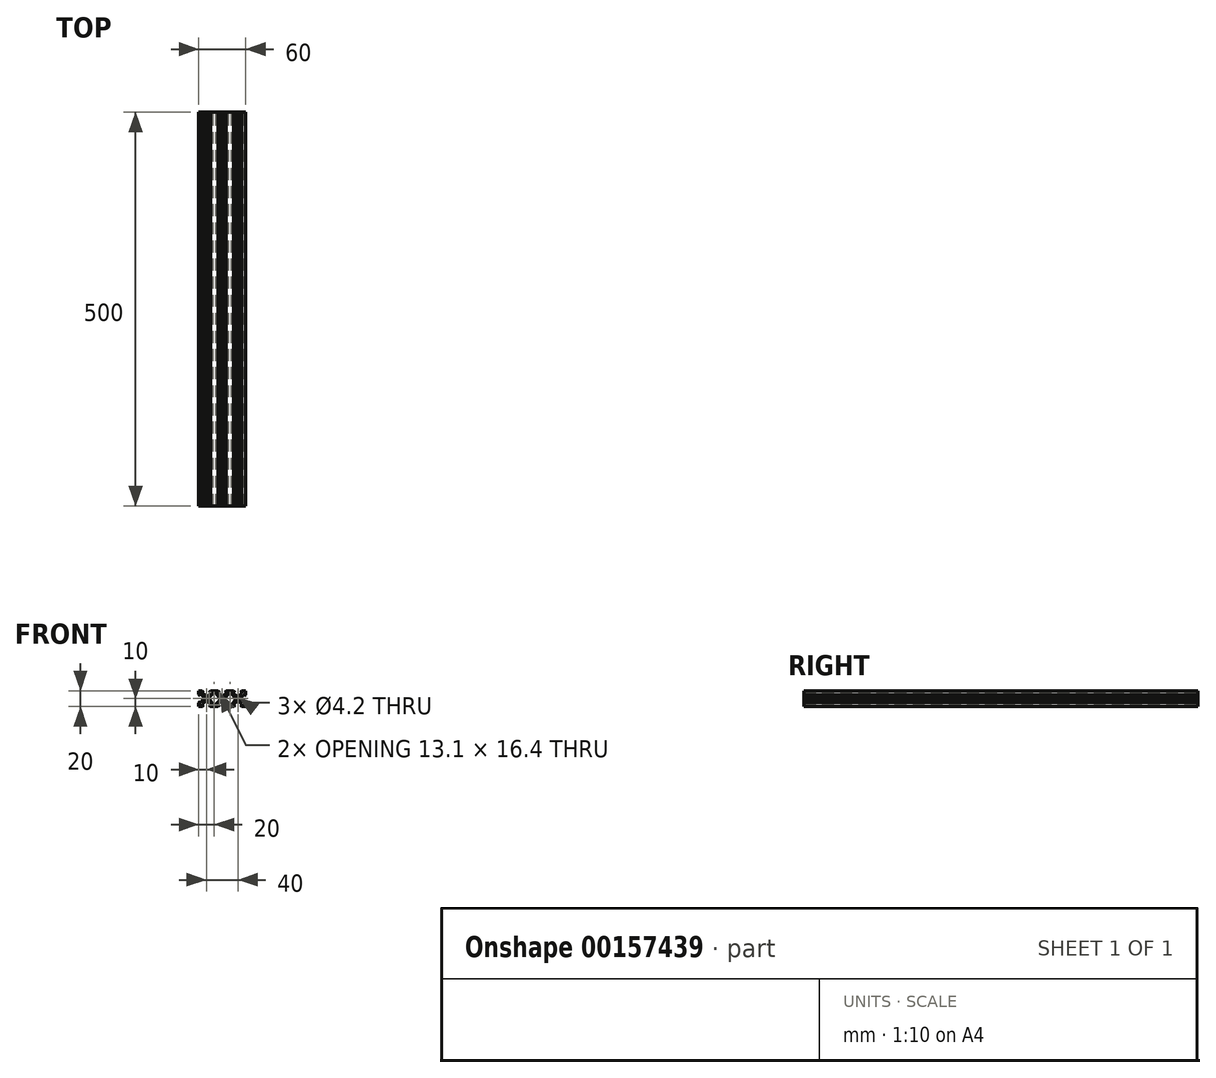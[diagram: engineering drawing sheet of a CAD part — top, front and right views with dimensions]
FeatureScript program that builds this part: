
annotation { "Feature Type Name" : "Feature", "Feature Type Description" : "" }
export const myFeature = defineFeature(function(context is Context, id is Id, definition is map)
    precondition{}
    {
        {
            var Q0;
            Q0=qCreatedBy(makeId("Front.planeOp"),FACE);
            var sketch = newSketch(context, id + "F0", { "sketchPlane" : qUnion([Q0])});
            skLineSegment(sketch, "E0.bottom", {"start": v(30, 10) * mm, "end": v(24.82, 10) * mm});
            skLineSegment(sketch, "E0.top", {"start": v(30, -10) * mm, "end": v(24.78, -10) * mm});
            skLineSegment(sketch, "E0.left", {"start": v(30, 10) * mm, "end": v(30, 4.8) * mm});
            skLineSegment(sketch, "E0.right", {"start": v(-30, 10) * mm, "end": v(-30, 5.17) * mm});
            skPoint(sketch, "E0.middle", {"position": v(0, 0) * mm});
            skLineSegment(sketch, "E1.0", {"start": v(-28.2, 8.2) * mm, "end": v(-28.2, 3.63) * mm});
            skLineSegment(sketch, "E1.1", {"start": v(28.2, 8.2) * mm, "end": v(23.56, 8.2) * mm});
            skLineSegment(sketch, "E1.2", {"start": v(28.2, 8.2) * mm, "end": v(28.2, 3.44) * mm});
            skLineSegment(sketch, "E1.3", {"start": v(28.2, -8.2) * mm, "end": v(23.52, -8.2) * mm});
            skCircle(sketch, "E2", {"center": v(0, 0) * mm, "radius": 2.1 * mm});
            skCircle(sketch, "E3", {"center": v(-20, 0) * mm, "radius": 2.1 * mm});
            skCircle(sketch, "E4", {"center": v(20, 0) * mm, "radius": 2.1 * mm});
            skLineSegment(sketch, "E5", {"start": v(-30, 5.17) * mm, "end": v(-28.2, 3.63) * mm});
            skLineSegment(sketch, "E6", {"start": v(-30, -5.22) * mm, "end": v(-28.2, -3.47) * mm});
            skLineSegment(sketch, "E7", {"start": v(-25.2, 10) * mm, "end": v(-23.47, 8.2) * mm});
            skLineSegment(sketch, "E8", {"start": v(-16.45, 8.2) * mm, "end": v(-14.84, 10) * mm});
            skLineSegment(sketch, "E9", {"start": v(-24.81, -10) * mm, "end": v(-23.55, -8.2) * mm});
            skLineSegment(sketch, "E10", {"start": v(-16.57, -8.2) * mm, "end": v(-15.34, -10) * mm});
            skLineSegment(sketch, "E11", {"start": v(3.5, 8.2) * mm, "end": v(5.22, 10) * mm});
            skLineSegment(sketch, "E12", {"start": v(-4.91, -10) * mm, "end": v(-3.52, -8.2) * mm});
            skLineSegment(sketch, "E13", {"start": v(3.53, -8.2) * mm, "end": v(5.18, -10) * mm});
            skLineSegment(sketch, "E14", {"start": v(14.8, 10) * mm, "end": v(16.37, 8.2) * mm});
            skLineSegment(sketch, "E15", {"start": v(23.56, 8.2) * mm, "end": v(24.82, 10) * mm});
            skLineSegment(sketch, "E16", {"start": v(15.3, -10) * mm, "end": v(16.45, -8.2) * mm});
            skLineSegment(sketch, "E17", {"start": v(23.52, -8.2) * mm, "end": v(24.78, -10) * mm});
            skLineSegment(sketch, "E18", {"start": v(28.2, -3.58) * mm, "end": v(30, -5.08) * mm});
            skLineSegment(sketch, "E19", {"start": v(28.2, 3.44) * mm, "end": v(30, 4.8) * mm});
            skLineSegment(sketch, "E20.bottom", {"start": v(-16.55, 3.45) * mm, "end": v(-23.45, 3.45) * mm});
            skLineSegment(sketch, "E20.top", {"start": v(-16.55, -3.45) * mm, "end": v(-23.45, -3.45) * mm});
            skLineSegment(sketch, "E20.left", {"start": v(-16.55, 3.45) * mm, "end": v(-16.55, -3.45) * mm});
            skLineSegment(sketch, "E20.right", {"start": v(-23.45, 3.45) * mm, "end": v(-23.45, -3.45) * mm});
            skLineSegment(sketch, "E21.bottom", {"start": v(3.45, 3.45) * mm, "end": v(-3.45, 3.45) * mm});
            skLineSegment(sketch, "E21.top", {"start": v(3.45, -3.45) * mm, "end": v(-3.45, -3.45) * mm});
            skLineSegment(sketch, "E21.left", {"start": v(3.45, 3.45) * mm, "end": v(3.45, -3.45) * mm});
            skLineSegment(sketch, "E21.right", {"start": v(-3.45, 3.45) * mm, "end": v(-3.45, -3.45) * mm});
            skLineSegment(sketch, "E22.bottom", {"start": v(23.45, 3.45) * mm, "end": v(16.55, 3.45) * mm});
            skLineSegment(sketch, "E22.top", {"start": v(23.45, -3.45) * mm, "end": v(16.55, -3.45) * mm});
            skLineSegment(sketch, "E22.left", {"start": v(23.45, 3.45) * mm, "end": v(23.45, -3.45) * mm});
            skLineSegment(sketch, "E22.right", {"start": v(16.55, 3.45) * mm, "end": v(16.55, -3.45) * mm});
            skLineSegment(sketch, "E23", {"start": v(-20, 2.1) * mm, "end": v(-44.26, 2.1) * mm, "construction": true});
            skPoint(sketch, "E23.startSnap0", {"position": v(-20, 3.45) * mm});
            skLineSegment(sketch, "E24", {"start": v(-19.99, -2.1) * mm, "end": v(-43.86, -2.1) * mm, "construction": true});
            skLineSegment(sketch, "E25.0", {"start": v(-26.56, 6.56) * mm, "end": v(-26.56, 5.22) * mm});
            skLineSegment(sketch, "E25.1", {"start": v(26.56, 6.56) * mm, "end": v(24.86, 6.56) * mm});
            skLineSegment(sketch, "E25.2", {"start": v(26.56, 6.56) * mm, "end": v(26.56, 4.87) * mm});
            skLineSegment(sketch, "E25.3", {"start": v(26.56, -6.56) * mm, "end": v(24.85, -6.56) * mm});
            skLineSegment(sketch, "E26", {"start": v(-25.16, 6.56) * mm, "end": v(-25.16, 8.2) * mm});
            skLineSegment(sketch, "E27", {"start": v(-26.56, 5.22) * mm, "end": v(-28.2, 5.22) * mm});
            skLineSegment(sketch, "E28", {"start": v(-25.16, 6.56) * mm, "end": v(-20.7, 3.45) * mm});
            skLineSegment(sketch, "E29", {"start": v(-26.56, 5.22) * mm, "end": v(-23.45, 2.06) * mm});
            skLineSegment(sketch, "E30", {"start": v(-26.56, -5.26) * mm, "end": v(-23.45, -0.51) * mm});
            skLineSegment(sketch, "E31", {"start": v(-24.87, -6.56) * mm, "end": v(-21.77, -3.45) * mm});
            skLineSegment(sketch, "E32", {"start": v(-26.56, -5.26) * mm, "end": v(-28.2, -5.26) * mm});
            skLineSegment(sketch, "E33", {"start": v(-24.87, -6.56) * mm, "end": v(-24.87, -8.2) * mm});
            skLineSegment(sketch, "E34", {"start": v(-14.83, 8.2) * mm, "end": v(-14.83, 6.56) * mm});
            skLineSegment(sketch, "E35", {"start": v(-14.83, 6.56) * mm, "end": v(-18, 3.45) * mm});
            skLineSegment(sketch, "E36", {"start": v(-16.55, 1.87) * mm, "end": v(-11.8, 6.56) * mm});
            skLineSegment(sketch, "E37", {"start": v(-3.48, 8.2) * mm, "end": v(-4.91, 10) * mm});
            skLineSegment(sketch, "E38", {"start": v(-19.34, -3.45) * mm, "end": v(-15.36, -6.56) * mm});
            skLineSegment(sketch, "E39", {"start": v(-15.36, -6.56) * mm, "end": v(-15.36, -8.2) * mm});
            skLineSegment(sketch, "E40", {"start": v(-16.55, -0.63) * mm, "end": v(-12.6, -6.56) * mm});
            skLineSegment(sketch, "E41", {"start": v(-1.9, 3.45) * mm, "end": v(-4.8, 6.56) * mm});
            skLineSegment(sketch, "E42", {"start": v(-4.8, 6.56) * mm, "end": v(-4.8, 8.2) * mm});
            skLineSegment(sketch, "E43", {"start": v(-3.45, 0.53) * mm, "end": v(-7.5, 6.56) * mm});
            skLineSegment(sketch, "E44", {"start": v(-3.45, -2.14) * mm, "end": v(-7.78, -6.56) * mm});
            skLineSegment(sketch, "E45", {"start": v(-1.46, -3.45) * mm, "end": v(-5.05, -6.56) * mm});
            skLineSegment(sketch, "E46", {"start": v(-5.05, -6.56) * mm, "end": v(-5.05, -8.2) * mm});
            skLineSegment(sketch, "E47", {"start": v(-12.6, -6.56) * mm, "end": v(-12.6, -8.2) * mm});
            skLineSegment(sketch, "E48", {"start": v(-7.78, -6.56) * mm, "end": v(-7.78, -8.2) * mm});
            skLineSegment(sketch, "E49", {"start": v(-7.5, 6.56) * mm, "end": v(-7.5, 8.2) * mm});
            skLineSegment(sketch, "E50", {"start": v(-11.8, 6.56) * mm, "end": v(-11.8, 8.2) * mm});
            skLineSegment(sketch, "E51", {"start": v(0.74, 3.45) * mm, "end": v(5.08, 6.56) * mm});
            skLineSegment(sketch, "E52", {"start": v(3.45, 0.52) * mm, "end": v(8.04, 6.56) * mm});
            skLineSegment(sketch, "E53", {"start": v(8.04, 6.56) * mm, "end": v(8.04, 8.2) * mm});
            skLineSegment(sketch, "E54", {"start": v(1.52, -3.45) * mm, "end": v(5.2, -6.56) * mm});
            skLineSegment(sketch, "E55", {"start": v(5.2, -6.56) * mm, "end": v(5.2, -8.2) * mm});
            skLineSegment(sketch, "E56", {"start": v(3.45, -1.7) * mm, "end": v(7.97, -6.56) * mm});
            skLineSegment(sketch, "E57", {"start": v(18.15, 3.45) * mm, "end": v(14.79, 6.56) * mm});
            skLineSegment(sketch, "E58", {"start": v(16.55, 0.58) * mm, "end": v(12.18, 6.56) * mm});
            skLineSegment(sketch, "E59", {"start": v(12.18, 6.56) * mm, "end": v(12.18, 8.2) * mm});
            skLineSegment(sketch, "E60", {"start": v(14.79, 6.56) * mm, "end": v(14.79, 8.2) * mm});
            skLineSegment(sketch, "E61", {"start": v(16.55, -2.05) * mm, "end": v(12.38, -6.56) * mm});
            skLineSegment(sketch, "E62", {"start": v(18.78, -3.45) * mm, "end": v(15.16, -6.56) * mm});
            skLineSegment(sketch, "E63", {"start": v(12.38, -6.56) * mm, "end": v(12.38, -8.2) * mm});
            skLineSegment(sketch, "E64", {"start": v(20.78, 3.45) * mm, "end": v(24.86, 6.56) * mm});
            skLineSegment(sketch, "E65", {"start": v(23.45, 0.43) * mm, "end": v(26.56, 4.87) * mm});
            skLineSegment(sketch, "E66", {"start": v(23.45, -1.97) * mm, "end": v(26.56, -5.05) * mm});
            skLineSegment(sketch, "E67", {"start": v(26.56, -5.05) * mm, "end": v(28.2, -5.05) * mm});
            skLineSegment(sketch, "E68", {"start": v(21.27, -3.45) * mm, "end": v(24.85, -6.56) * mm});
            skLineSegment(sketch, "E69", {"start": v(24.85, -6.56) * mm, "end": v(24.85, -8.2) * mm});
            skLineSegment(sketch, "E70.trimOffspring", {"start": v(-25.2, 10) * mm, "end": v(-30, 10) * mm});
            skLineSegment(sketch, "E71.trimOffspring", {"start": v(-23.47, 8.2) * mm, "end": v(-28.2, 8.2) * mm});
            skLineSegment(sketch, "E72.trimOffspring", {"start": v(-25.16, 6.56) * mm, "end": v(-26.56, 6.56) * mm});
            skLineSegment(sketch, "E73.trimOffspring", {"start": v(-28.2, -3.47) * mm, "end": v(-28.2, -8.2) * mm});
            skLineSegment(sketch, "E74.trimOffspring", {"start": v(-30, -5.22) * mm, "end": v(-30, -10) * mm});
            skLineSegment(sketch, "E75.trimOffspring", {"start": v(-26.56, -5.26) * mm, "end": v(-26.56, -6.56) * mm});
            skLineSegment(sketch, "E76.trimOffspring", {"start": v(-11.8, 6.56) * mm, "end": v(-14.83, 6.56) * mm});
            skLineSegment(sketch, "E77.trimOffspring", {"start": v(-12.6, -6.56) * mm, "end": v(-15.36, -6.56) * mm});
            skLineSegment(sketch, "E78.trimOffspring", {"start": v(-24.87, -6.56) * mm, "end": v(-26.56, -6.56) * mm});
            skLineSegment(sketch, "E79.trimOffspring", {"start": v(-23.55, -8.2) * mm, "end": v(-28.2, -8.2) * mm});
            skLineSegment(sketch, "E80.trimOffspring", {"start": v(-24.81, -10) * mm, "end": v(-30, -10) * mm});
            skLineSegment(sketch, "E81.trimOffspring", {"start": v(-4.91, 10) * mm, "end": v(-14.84, 10) * mm});
            skLineSegment(sketch, "E82", {"start": v(5.08, 6.56) * mm, "end": v(5.08, 8.2) * mm});
            skLineSegment(sketch, "E83.trimOffspring", {"start": v(-3.48, 8.2) * mm, "end": v(-16.45, 8.2) * mm});
            skLineSegment(sketch, "E84.trimOffspring", {"start": v(-4.8, 6.56) * mm, "end": v(-7.5, 6.56) * mm});
            skLineSegment(sketch, "E85.trimOffspring", {"start": v(8.04, 6.56) * mm, "end": v(5.08, 6.56) * mm});
            skLineSegment(sketch, "E86.trimOffspring", {"start": v(7.97, -6.56) * mm, "end": v(5.2, -6.56) * mm});
            skLineSegment(sketch, "E87.trimOffspring", {"start": v(-4.91, -10) * mm, "end": v(-15.34, -10) * mm});
            skLineSegment(sketch, "E88.trimOffspring", {"start": v(-3.52, -8.2) * mm, "end": v(-16.57, -8.2) * mm});
            skLineSegment(sketch, "E89.trimOffspring", {"start": v(-5.05, -6.56) * mm, "end": v(-7.78, -6.56) * mm});
            skLineSegment(sketch, "E90.trimOffspring", {"start": v(15.3, -10) * mm, "end": v(5.18, -10) * mm});
            skLineSegment(sketch, "E91", {"start": v(15.16, -6.56) * mm, "end": v(15.16, -8.2) * mm});
            skLineSegment(sketch, "E92.trimOffspring", {"start": v(16.45, -8.2) * mm, "end": v(3.53, -8.2) * mm});
            skLineSegment(sketch, "E93.trimOffspring", {"start": v(15.16, -6.56) * mm, "end": v(12.38, -6.56) * mm});
            skLineSegment(sketch, "E94.trimOffspring", {"start": v(30, -5.08) * mm, "end": v(30, -10) * mm});
            skLineSegment(sketch, "E95.trimOffspring", {"start": v(28.2, -3.58) * mm, "end": v(28.2, -8.2) * mm});
            skLineSegment(sketch, "E96.trimOffspring", {"start": v(26.56, -5.05) * mm, "end": v(26.56, -6.56) * mm});
            skLineSegment(sketch, "E97", {"start": v(24.86, 6.56) * mm, "end": v(24.86, 8.2) * mm});
            skLineSegment(sketch, "E98", {"start": v(26.56, 4.87) * mm, "end": v(28.2, 4.87) * mm});
            skLineSegment(sketch, "E99.trimOffspring", {"start": v(14.8, 10) * mm, "end": v(5.22, 10) * mm});
            skLineSegment(sketch, "E100.trimOffspring", {"start": v(16.37, 8.2) * mm, "end": v(3.5, 8.2) * mm});
            skLineSegment(sketch, "E101.trimOffspring", {"start": v(14.79, 6.56) * mm, "end": v(12.18, 6.56) * mm});
            skLineSegment(sketch, "E102", {"start": v(7.97, -6.56) * mm, "end": v(7.97, -8.2) * mm});
            skSolve(sketch);
        }
        {
            var Q0;
            Q0=makeQuery(id+"F0.imprint","IMPRINT",FACE,{"disambiguationData":[TD([[makeQuery(id+"F0.imprint","IMPRINT",EDGE,{"derivedFrom":sQuery(id+"F0.wireOp",EDGE,"E0.bottom")}),1.0]])]});
            var Q1;
            Q1=makeQuery(id+"F0.imprint","IMPRINT",FACE,{"disambiguationData":[TD([[makeQuery(id+"F0.imprint","IMPRINT",EDGE,{"derivedFrom":sQuery(id+"F0.wireOp",EDGE,"E25.1")}),-1.0]])]});
            var Q2;
            Q2=makeQuery(id+"F0.imprint","IMPRINT",FACE,{"disambiguationData":[TD([[makeQuery(id+"F0.imprint","IMPRINT",EDGE,{"derivedFrom":sQuery(id+"F0.wireOp",EDGE,"E25.1")}),1.0]])]});
            var Q3;
            {var subQ1=sQuery(id+"F0.wireOp",EDGE,"E25.3");Q3=makeQuery(id+"F0.imprint","IMPRINT",FACE,{"disambiguationData":[TD([[makeQuery(id+"F0.imprint","IMPRINT",EDGE,{"derivedFrom":subQ1}),1.0]])]});}
            var Q4;
            Q4=makeQuery(id+"F0.imprint","IMPRINT",FACE,{"disambiguationData":[TD([[makeQuery(id+"F0.imprint","IMPRINT",EDGE,{"derivedFrom":sQuery(id+"F0.wireOp",EDGE,"E0.top")}),-1.0]])]});
            var Q5;
            Q5=makeQuery(id+"F0.imprint","IMPRINT",FACE,{"disambiguationData":[TD([[makeQuery(id+"F0.imprint","IMPRINT",EDGE,{"derivedFrom":sQuery(id+"F0.wireOp",EDGE,"E25.3")}),-1.0]])]});
            var Q6;
            Q6=makeQuery(id+"F0.imprint","IMPRINT",FACE,{"disambiguationData":[TD([[makeQuery(id+"F0.imprint","IMPRINT",EDGE,{"derivedFrom":sQuery(id+"F0.wireOp",EDGE,"E4")}),-1.0]])]});
            var Q7;
            {var subQ1=sQuery(id+"F0.wireOp",EDGE,"E57");Q7=makeQuery(id+"F0.imprint","IMPRINT",FACE,{"disambiguationData":[TD([[makeQuery(id+"F0.imprint","IMPRINT",EDGE,{"derivedFrom":subQ1}),1.0]])]});}
            var Q8;
            {var subQ4=sQuery(id+"F0.wireOp",EDGE,"E60");Q8=makeQuery(id+"F0.imprint","IMPRINT",FACE,{"disambiguationData":[TD([[makeQuery(id+"F0.imprint","IMPRINT",EDGE,{"derivedFrom":subQ4}),1.0]])]});}
            var Q9;
            {var subQ3=sQuery(id+"F0.wireOp",EDGE,"E11");Q9=makeQuery(id+"F0.imprint","IMPRINT",FACE,{"disambiguationData":[TD([[makeQuery(id+"F0.imprint","IMPRINT",EDGE,{"derivedFrom":subQ3}),-1.0]])]});}
            var Q10;
            {var subQ0=sQuery(id+"F0.wireOp",EDGE,"E53");Q10=makeQuery(id+"F0.imprint","IMPRINT",FACE,{"disambiguationData":[TD([[makeQuery(id+"F0.imprint","IMPRINT",EDGE,{"derivedFrom":subQ0}),1.0]])]});}
            var Q11;
            {var subQ1=sQuery(id+"F0.wireOp",EDGE,"E51");Q11=makeQuery(id+"F0.imprint","IMPRINT",FACE,{"disambiguationData":[TD([[makeQuery(id+"F0.imprint","IMPRINT",EDGE,{"derivedFrom":subQ1}),-1.0]])]});}
            var Q12;
            {var subQ4=sQuery(id+"F0.wireOp",EDGE,"E61");Q12=makeQuery(id+"F0.imprint","IMPRINT",FACE,{"disambiguationData":[TD([[makeQuery(id+"F0.imprint","IMPRINT",EDGE,{"derivedFrom":subQ4}),1.0]])]});}
            var Q13;
            {var subQ0=sQuery(id+"F0.wireOp",EDGE,"E63");Q13=makeQuery(id+"F0.imprint","IMPRINT",FACE,{"disambiguationData":[TD([[makeQuery(id+"F0.imprint","IMPRINT",EDGE,{"derivedFrom":subQ0}),1.0]])]});}
            var Q14;
            {var subQ3=sQuery(id+"F0.wireOp",EDGE,"E13");Q14=makeQuery(id+"F0.imprint","IMPRINT",FACE,{"disambiguationData":[TD([[makeQuery(id+"F0.imprint","IMPRINT",EDGE,{"derivedFrom":subQ3}),1.0]])]});}
            var Q15;
            {var subQ0=sQuery(id+"F0.wireOp",EDGE,"E86.trimOffspring");Q15=makeQuery(id+"F0.imprint","IMPRINT",FACE,{"disambiguationData":[TD([[makeQuery(id+"F0.imprint","IMPRINT",EDGE,{"derivedFrom":subQ0}),1.0]])]});}
            var Q16;
            {var subQ1=sQuery(id+"F0.wireOp",EDGE,"E54");Q16=makeQuery(id+"F0.imprint","IMPRINT",FACE,{"disambiguationData":[TD([[makeQuery(id+"F0.imprint","IMPRINT",EDGE,{"derivedFrom":subQ1}),1.0]])]});}
            var Q17;
            Q17=makeQuery(id+"F0.imprint","IMPRINT",FACE,{"disambiguationData":[TD([[makeQuery(id+"F0.imprint","IMPRINT",EDGE,{"derivedFrom":sQuery(id+"F0.wireOp",EDGE,"E2")}),-1.0]])]});
            var Q18;
            {var subQ0=sQuery(id+"F0.wireOp",EDGE,"E41");Q18=makeQuery(id+"F0.imprint","IMPRINT",FACE,{"disambiguationData":[TD([[makeQuery(id+"F0.imprint","IMPRINT",EDGE,{"derivedFrom":subQ0}),1.0]])]});}
            var Q19;
            {var subQ0=sQuery(id+"F0.wireOp",EDGE,"E42");Q19=makeQuery(id+"F0.imprint","IMPRINT",FACE,{"disambiguationData":[TD([[makeQuery(id+"F0.imprint","IMPRINT",EDGE,{"derivedFrom":subQ0}),1.0]])]});}
            var Q20;
            {var subQ5=sQuery(id+"F0.wireOp",EDGE,"E8");Q20=makeQuery(id+"F0.imprint","IMPRINT",FACE,{"disambiguationData":[TD([[makeQuery(id+"F0.imprint","IMPRINT",EDGE,{"derivedFrom":subQ5}),-1.0]])]});}
            var Q21;
            {var subQ0=sQuery(id+"F0.wireOp",EDGE,"E34");Q21=makeQuery(id+"F0.imprint","IMPRINT",FACE,{"disambiguationData":[TD([[makeQuery(id+"F0.imprint","IMPRINT",EDGE,{"derivedFrom":subQ0}),1.0]])]});}
            var Q22;
            {var subQ0=sQuery(id+"F0.wireOp",EDGE,"E35");Q22=makeQuery(id+"F0.imprint","IMPRINT",FACE,{"disambiguationData":[TD([[makeQuery(id+"F0.imprint","IMPRINT",EDGE,{"derivedFrom":subQ0}),1.0]])]});}
            var Q23;
            {var subQ1=sQuery(id+"F0.wireOp",EDGE,"E44");Q23=makeQuery(id+"F0.imprint","IMPRINT",FACE,{"disambiguationData":[TD([[makeQuery(id+"F0.imprint","IMPRINT",EDGE,{"derivedFrom":subQ1}),1.0]])]});}
            var Q24;
            {var subQ0=sQuery(id+"F0.wireOp",EDGE,"E46");Q24=makeQuery(id+"F0.imprint","IMPRINT",FACE,{"disambiguationData":[TD([[makeQuery(id+"F0.imprint","IMPRINT",EDGE,{"derivedFrom":subQ0}),-1.0]])]});}
            var Q25;
            {var subQ3=sQuery(id+"F0.wireOp",EDGE,"E10");Q25=makeQuery(id+"F0.imprint","IMPRINT",FACE,{"disambiguationData":[TD([[makeQuery(id+"F0.imprint","IMPRINT",EDGE,{"derivedFrom":subQ3}),1.0]])]});}
            var Q26;
            {var subQ0=sQuery(id+"F0.wireOp",EDGE,"E39");Q26=makeQuery(id+"F0.imprint","IMPRINT",FACE,{"disambiguationData":[TD([[makeQuery(id+"F0.imprint","IMPRINT",EDGE,{"derivedFrom":subQ0}),1.0]])]});}
            var Q27;
            {var subQ0=sQuery(id+"F0.wireOp",EDGE,"E38");Q27=makeQuery(id+"F0.imprint","IMPRINT",FACE,{"disambiguationData":[TD([[makeQuery(id+"F0.imprint","IMPRINT",EDGE,{"derivedFrom":subQ0}),1.0]])]});}
            var Q28;
            Q28=makeQuery(id+"F0.imprint","IMPRINT",FACE,{"disambiguationData":[TD([[makeQuery(id+"F0.imprint","IMPRINT",EDGE,{"derivedFrom":sQuery(id+"F0.wireOp",EDGE,"E3")}),-1.0]])]});
            var Q29;
            Q29=makeQuery(id+"F0.imprint","IMPRINT",FACE,{"disambiguationData":[TD([[makeQuery(id+"F0.imprint","IMPRINT",EDGE,{"derivedFrom":sQuery(id+"F0.wireOp",EDGE,"E25.0")}),1.0]])]});
            var Q30;
            {var subQ1=sQuery(id+"F0.wireOp",EDGE,"E30");Q30=makeQuery(id+"F0.imprint","IMPRINT",FACE,{"disambiguationData":[TD([[makeQuery(id+"F0.imprint","IMPRINT",EDGE,{"derivedFrom":subQ1}),-1.0]])]});}
            var Q31;
            Q31=makeQuery(id+"F0.imprint","IMPRINT",FACE,{"disambiguationData":[TD([[makeQuery(id+"F0.imprint","IMPRINT",EDGE,{"derivedFrom":sQuery(id+"F0.wireOp",EDGE,"E25.0")}),-1.0]])]});
            var Q32;
            Q32=makeQuery(id+"F0.imprint","IMPRINT",FACE,{"disambiguationData":[TD([[makeQuery(id+"F0.imprint","IMPRINT",EDGE,{"derivedFrom":sQuery(id+"F0.wireOp",EDGE,"E0.right")}),1.0]])]});
            var Q33;
            {var subQ1=sQuery(id+"F0.wireOp",EDGE,"E32");Q33=makeQuery(id+"F0.imprint","IMPRINT",FACE,{"disambiguationData":[TD([[makeQuery(id+"F0.imprint","IMPRINT",EDGE,{"derivedFrom":subQ1}),1.0]])]});}
            var Q34;
            {var subQ4=sQuery(id+"F0.wireOp",EDGE,"E6");Q34=makeQuery(id+"F0.imprint","IMPRINT",FACE,{"disambiguationData":[TD([[makeQuery(id+"F0.imprint","IMPRINT",EDGE,{"derivedFrom":subQ4}),-1.0]])]});}
            extrude(context, id + "F1", {"entities" : qUnion([Q0, Q1, Q2, Q3, Q4, Q5, Q6, Q7, Q8, Q9, Q10, Q11, Q12, Q13, Q14, Q15, Q16, Q17, Q18, Q19, Q20, Q21, Q22, Q23, Q24, Q25, Q26, Q27, Q28, Q29, Q30, Q31, Q32, Q33, Q34]), "depth" : 500 * mm});
        }
    });
